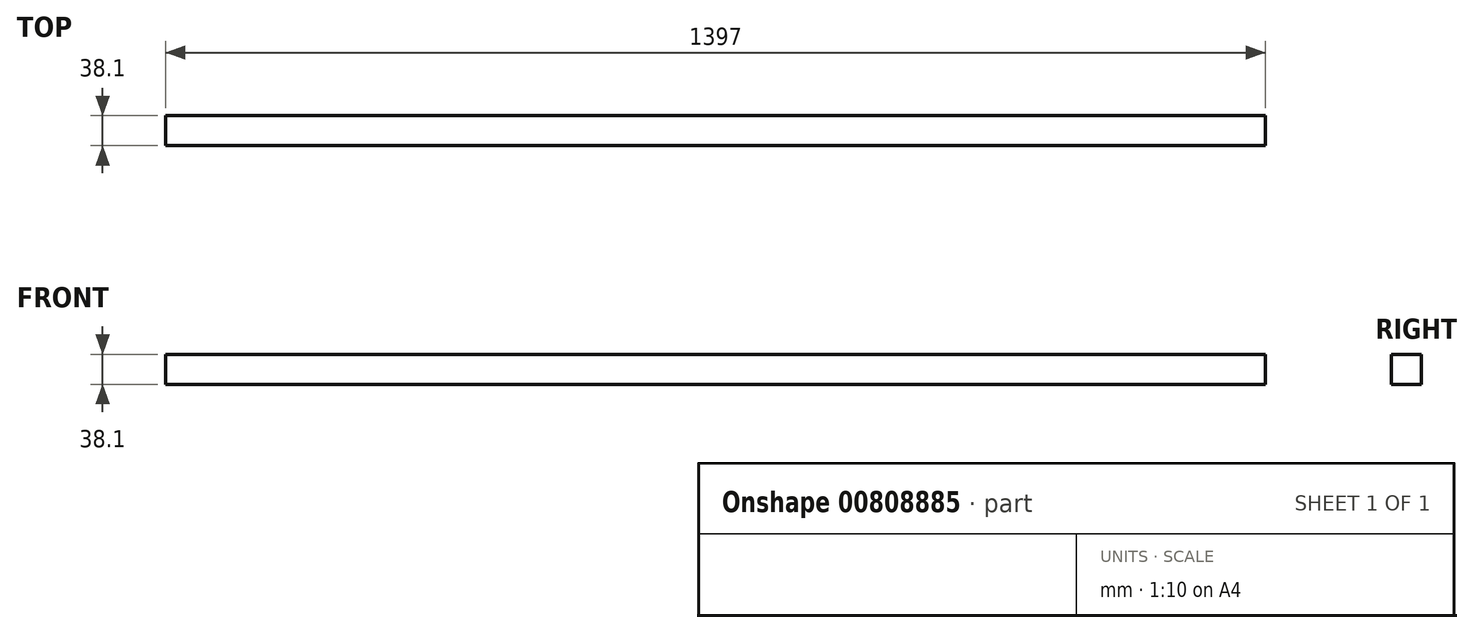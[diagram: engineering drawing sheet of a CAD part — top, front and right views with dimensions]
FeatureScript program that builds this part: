
annotation { "Feature Type Name" : "Feature", "Feature Type Description" : "" }
export const myFeature = defineFeature(function(context is Context, id is Id, definition is map)
    precondition{}
    {
        {
            var Q0;
            Q0=qCreatedBy(makeId("Top.planeOp"),FACE);
            var sketch = newSketch(context, id + "F0", { "sketchPlane" : qUnion([Q0])});
            skLineSegment(sketch, "E0.bottom", {"start": v(-616.3, 10.76) * mm, "end": v(780.7, 10.76) * mm});
            skLineSegment(sketch, "E0.top", {"start": v(-616.3, -27.34) * mm, "end": v(780.7, -27.34) * mm});
            skLineSegment(sketch, "E0.left", {"start": v(-616.3, 10.76) * mm, "end": v(-616.3, -27.34) * mm});
            skLineSegment(sketch, "E0.right", {"start": v(780.7, 10.76) * mm, "end": v(780.7, -27.34) * mm});
            skSolve(sketch);
        }
        {
            var Q0;
            Q0=qSketchRegion(id+"F0",true);
            extrude(context, id + "F1", {"entities" : qUnion([Q0]), "depth" : 38.1 * mm, "offsetDistance" : 25.4 * mm});
        }
    });
